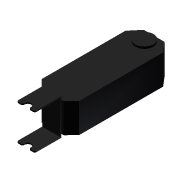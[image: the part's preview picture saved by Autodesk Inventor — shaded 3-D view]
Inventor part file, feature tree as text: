
AUTODESK INVENTOR PART (.ipt)
format: ipt  version: 2012 (Build 160160000, 160)  size: 148,480 bytes
history: native  units: mm
features: extrude x5, sketch x4
ambient origin geometry x8: Origin, YZ Plane, XZ Plane, XY Plane, X Axis, Y Axis, Z Axis, Center Point
bodies: Solid1 (feature_tree)
feature tree (9):
  sketch  "Sketch1"  dims[d0=22.0mm d1=36.0mm d2=0.0mm]
  extrude  "Extrusion1"  Depth=36.0mm TaperAngle=0.0deg
  extrude  "Extrusion2"  Depth=22.0mm
  extrude  "Extrusion3"  Depth=1.5mm TaperAngle=0.0deg
  extrude  "Extrusion4"  Depth=1.5mm
  extrude  "Extrusion5"  Depth=32.0mm TaperAngle=0.0deg
  sketch  "Sketch2"  dims[d3=41.0mm d4=0.0mm d5=22.0mm]
  sketch  "Sketch3"  dims[d6=44.0mm d7=1.5mm d8=0.0mm]
  sketch  "Sketch4"  dims[d9=1.5mm d10=1.5mm d11=32.0mm d12=0.0mm d13=32.0mm d14=0.0mm d16=22.0mm]
